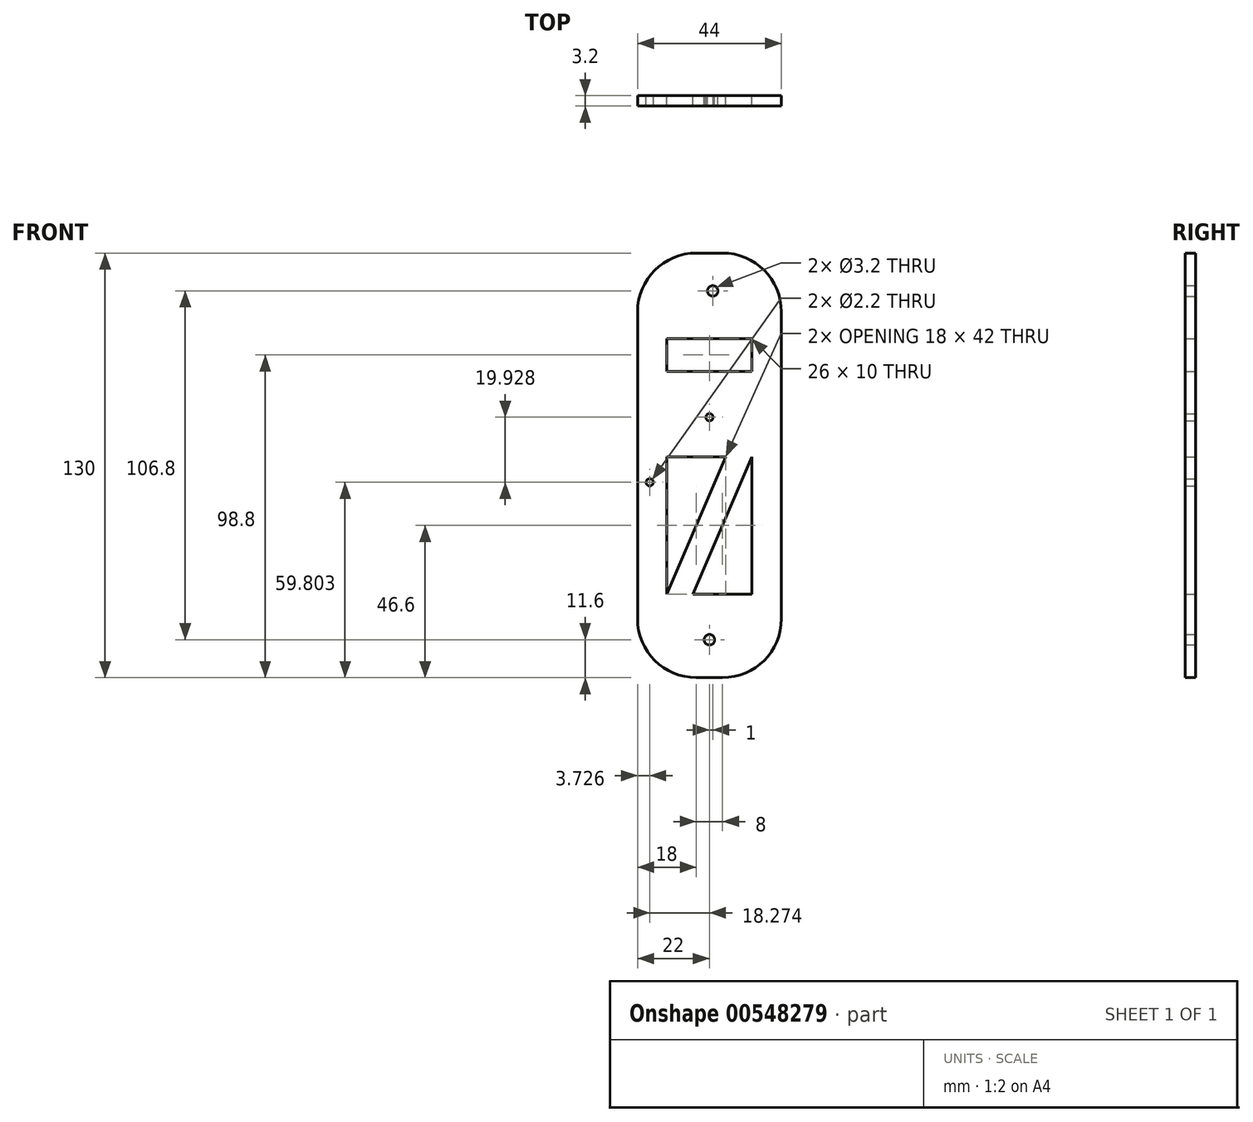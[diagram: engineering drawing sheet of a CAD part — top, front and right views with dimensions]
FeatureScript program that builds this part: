
annotation { "Feature Type Name" : "Feature", "Feature Type Description" : "" }
export const myFeature = defineFeature(function(context is Context, id is Id, definition is map)
    precondition{}
    {
        {
            var Q0;
            Q0=qCreatedBy(makeId("Front.planeOp"),FACE);
            var sketch = newSketch(context, id + "F0", { "sketchPlane" : qUnion([Q0])});
            skLineSegment(sketch, "E0.bottom", {"start": v(-4, 0) * mm, "end": v(4, 0) * mm});
            skLineSegment(sketch, "E0.top", {"start": v(-4, 130) * mm, "end": v(4, 130) * mm});
            skLineSegment(sketch, "E0.left", {"start": v(-22, 18) * mm, "end": v(-22, 112) * mm});
            skLineSegment(sketch, "E0.right", {"start": v(22, 18) * mm, "end": v(22, 112) * mm});
            skPoint(sketch, "E1.visualSharp", {"position": v(-22, 130) * mm});
            skArc(sketch, "E1.filletArc", {"start": v(-4, 130) * mm, "mid": v(-16.73, 124.73) * mm, "end": v(-22, 112) * mm});
            skPoint(sketch, "E2.visualSharp", {"position": v(22, 130) * mm});
            skArc(sketch, "E2.filletArc", {"start": v(22, 112) * mm, "mid": v(16.73, 124.73) * mm, "end": v(4, 130) * mm});
            skPoint(sketch, "E3.visualSharp", {"position": v(-22, 0) * mm});
            skArc(sketch, "E3.filletArc", {"start": v(-22, 18) * mm, "mid": v(-16.73, 5.27) * mm, "end": v(-4, 0) * mm});
            skPoint(sketch, "E4.visualSharp", {"position": v(22, 0) * mm});
            skArc(sketch, "E4.filletArc", {"start": v(4, 0) * mm, "mid": v(16.73, 5.27) * mm, "end": v(22, 18) * mm});
            skCircle(sketch, "E5", {"center": v(1, 118.4) * mm, "radius": 1.6 * mm});
            skCircle(sketch, "E6", {"center": v(0, 11.6) * mm, "radius": 1.6 * mm});
            skCircle(sketch, "E7", {"center": v(-18.27, 59.8) * mm, "radius": 1.1 * mm});
            skLineSegment(sketch, "E8.bottom", {"start": v(-13, 25.6) * mm, "end": v(13, 25.6) * mm});
            skLineSegment(sketch, "E8.top", {"start": v(-13, 67.6) * mm, "end": v(13, 67.6) * mm});
            skLineSegment(sketch, "E8.left", {"start": v(-13, 25.6) * mm, "end": v(-13, 67.6) * mm});
            skLineSegment(sketch, "E8.right", {"start": v(13, 25.6) * mm, "end": v(13, 67.6) * mm});
            skLineSegment(sketch, "E9", {"start": v(-13, 25.6) * mm, "end": v(5, 67.6) * mm});
            skLineSegment(sketch, "E10", {"start": v(13, 67.6) * mm, "end": v(-5, 25.6) * mm});
            skLineSegment(sketch, "E11.bottom", {"start": v(-13, 103.8) * mm, "end": v(13, 103.8) * mm});
            skLineSegment(sketch, "E11.top", {"start": v(-13, 93.8) * mm, "end": v(13, 93.8) * mm});
            skLineSegment(sketch, "E11.left", {"start": v(-13, 103.8) * mm, "end": v(-13, 93.8) * mm});
            skLineSegment(sketch, "E11.right", {"start": v(13, 103.8) * mm, "end": v(13, 93.8) * mm});
            skCircle(sketch, "E12", {"center": v(0, 79.73) * mm, "radius": 1.1 * mm});
            skSolve(sketch);
        }
        {
            var Q0;
            Q0=makeQuery(id+"F0.imprint","IMPRINT",FACE,{"disambiguationData":[TD([[makeQuery(id+"F0.imprint","IMPRINT",EDGE,{"derivedFrom":sQuery(id+"F0.wireOp",EDGE,"E0.bottom")}),1.0]])]});
            var Q1;
            {var subQ0=sQuery(id+"F0.wireOp",EDGE,"E9");Q1=makeQuery(id+"F0.imprint","IMPRINT",FACE,{"disambiguationData":[TD([[makeQuery(id+"F0.imprint","IMPRINT",EDGE,{"derivedFrom":subQ0}),-1.0]])]});}
            extrude(context, id + "F1", {"entities" : qUnion([Q0, Q1]), "depth" : 3.2 * mm, "offsetDistance" : 25 * mm});
        }
    });
